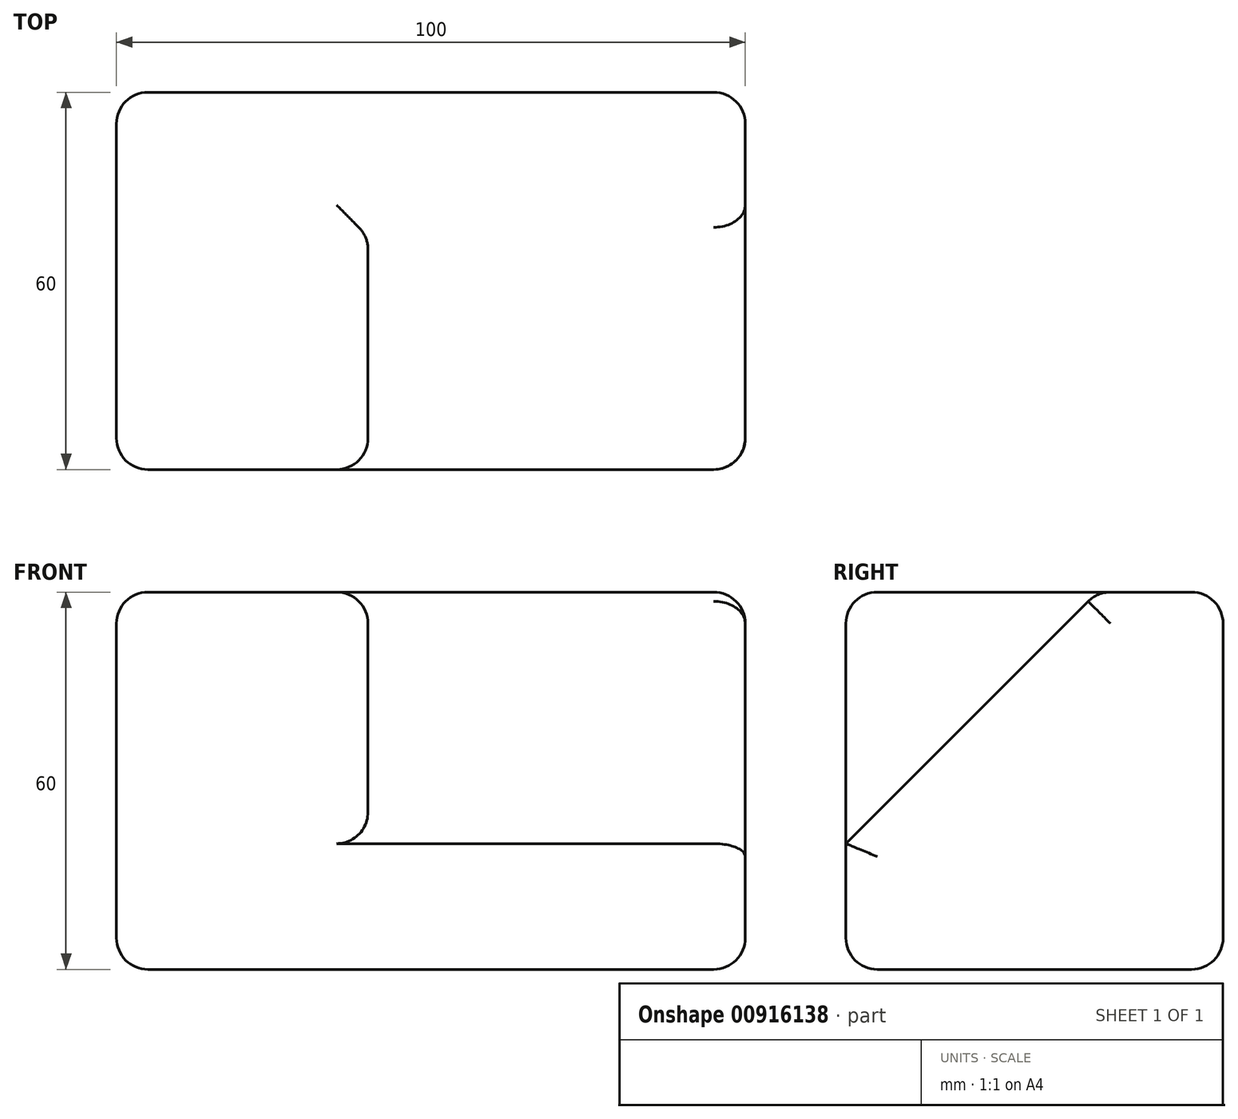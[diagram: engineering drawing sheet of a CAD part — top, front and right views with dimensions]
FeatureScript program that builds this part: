
annotation { "Feature Type Name" : "Feature", "Feature Type Description" : "" }
export const myFeature = defineFeature(function(context is Context, id is Id, definition is map)
    precondition{}
    {
        {
            var Q0;
            Q0=qCreatedBy(makeId("Top.planeOp"),FACE);
            var sketch = newSketch(context, id + "F0", { "sketchPlane" : qUnion([Q0])});
            skLineSegment(sketch, "E0.right", {"start": v(2540, 0) * mm, "end": v(2540, -51.36) * mm});
            skLineSegment(sketch, "E1.bottom", {"start": v(0, 0) * mm, "end": v(100, 0) * mm});
            skLineSegment(sketch, "E1.top", {"start": v(0, -60) * mm, "end": v(100, -60) * mm});
            skLineSegment(sketch, "E1.left", {"start": v(0, 0) * mm, "end": v(0, -60) * mm});
            skLineSegment(sketch, "E1.right", {"start": v(100, 0) * mm, "end": v(100, -60) * mm});
            skSolve(sketch);
        }
        {
            var Q0;
            Q0 = qSketchRegion(id + "F0", true);
            var Q1;
            Q1=makeQuery(id+"F0.imprint","IMPRINT",FACE,{"disambiguationData":[TD([[makeQuery(id+"F0.imprint","IMPRINT",EDGE,{"derivedFrom":sQuery(id+"F0.wireOp",EDGE,"E1.bottom")}),-1.0]])]});
            extrude(context, id + "F1", {"entities" : qUnion([Q0, Q1]), "depth" : 20 * mm, "offsetDistance" : 25 * mm});
        }
        {
            var Q0;
            Q0=makeQuery(id+"F1.opExtrude","CAP_FACE",FACE,{"disambiguationData":[OSD([sQuery(id+"F0.wireOp",EDGE,"E1.bottom"),sQuery(id+"F0.wireOp",EDGE,"E1.top"),sQuery(id+"F0.wireOp",EDGE,"E1.left"),sQuery(id+"F0.wireOp",EDGE,"E1.right")])],"isStart":false});
            var sketch = newSketch(context, id + "F2", { "sketchPlane" : qUnion([Q0])});
            skLineSegment(sketch, "E2", {"start": v(100, -20) * mm, "end": v(40, -20) * mm});
            skLineSegment(sketch, "E3", {"start": v(40, -20) * mm, "end": v(40, -60) * mm});
            skPoint(sketch, "E3.endSnap0", {"position": v(50, -60) * mm});
            skSolve(sketch);
        }
        {
            var Q0;
            Q0 = qSketchRegion(id + "F2", true);
            var Q1;
            {var subQ3=sQuery(id+"F2.wireOp",EDGE,"E2");Q1=makeQuery(id+"F2.imprint","IMPRINT",FACE,{"disambiguationData":[TD([[makeQuery(id+"F2.imprint","IMPRINT",EDGE,{"derivedFrom":subQ3}),-1.0]])]});}
            extrude(context, id + "F3", {"entities" : qUnion([Q0, Q1]), "operationType" : NewBodyOperationType.ADD, "depth" : 40 * mm, "offsetDistance" : 25 * mm});
        }
        {
            var Q0;
            Q0=makeQuery(id+"F3.opExtrude","SWEPT_FACE",FACE,{"disambiguationData":[OSD([sQuery(id+"F2.wireOp",EDGE,"E3")])]});
            var sketch = newSketch(context, id + "F4", { "sketchPlane" : qUnion([Q0])});
            skLineSegment(sketch, "E4", {"start": v(-60, 20) * mm, "end": v(-20, 60) * mm});
            skSolve(sketch);
        }
        {
            var Q0;
            Q0=makeQuery(id+"F4.imprint","IMPRINT",FACE,{"disambiguationData":[TD([[makeQuery(id+"F4.imprint","IMPRINT",EDGE,{"derivedFrom":sQuery(id+"F4.wireOp",EDGE,"E4")}),-1.0]])]});
            extrude(context, id + "F5", {"entities" : qUnion([Q0]), "operationType" : NewBodyOperationType.ADD, "depth" : 60 * mm, "offsetDistance" : 25 * mm});
        }
        {
            var Q0;
            Q0=makeQuery(id+"F3.opExtrude","CAP_EDGE",EDGE,{"disambiguationData":[OSD([sQuery(id+"F0.wireOp",EDGE,"E1.top")])],"isStart":false});
            var Q1;
            Q1=makeQuery(id+"F3.opExtrude","SWEPT_EDGE",EDGE,{"disambiguationData":[OSD([sQuery(id+"F0.wireOp",EDGE,"E1.top"),sQuery(id+"F2.wireOp",EDGE,"E3")])]});
            var Q2;
            Q2=makeQuery(id+"F3.opExtrude","CAP_EDGE",EDGE,{"disambiguationData":[OSD([sQuery(id+"F2.wireOp",EDGE,"E3")])],"isStart":false});
            var Q3;
            Q3=makeQuery(id+"F5.opExtrude","CAP_EDGE",EDGE,{"disambiguationData":[OSD([sQuery(id+"F4.wireOp",EDGE,"E4")])],"isStart":true});
            var Q4;
            Q4=makeQuery(id+"F5.opExtrude","CAP_EDGE",EDGE,{"disambiguationData":[OSD([sQuery(id+"F4.wireOp",EDGE,"E4")])],"isStart":false});
            var Q5;
            Q5=makeQuery(id+"F1.opExtrude","SWEPT_EDGE",EDGE,{"disambiguationData":[OSD([sQuery(id+"F0.wireOp",EDGE,"E1.top"),sQuery(id+"F0.wireOp",EDGE,"E1.right")])]});
            var Q6;
            Q6=makeQuery(id+"F1.opExtrude","CAP_EDGE",EDGE,{"disambiguationData":[OSD([sQuery(id+"F0.wireOp",EDGE,"E1.right")])],"isStart":true});
            var Q7;
            Q7=makeQuery(id+"F1.opExtrude","CAP_EDGE",EDGE,{"disambiguationData":[OSD([sQuery(id+"F0.wireOp",EDGE,"E1.top")])],"isStart":true});
            var Q8;
            Q8=makeQuery(id+"F3.opExtrude","CAP_EDGE",EDGE,{"disambiguationData":[OSD([sQuery(id+"F0.wireOp",EDGE,"E1.bottom")])],"isStart":false});
            var Q9;
            Q9=makeQuery(id+"F3.opExtrude","CAP_EDGE",EDGE,{"disambiguationData":[OSD([sQuery(id+"F0.wireOp",EDGE,"E1.left")])],"isStart":false});
            var Q10;
            {var subQ0=sQuery(id+"F0.wireOp",EDGE,"E1.right");var subQ1=sQuery(id+"F0.wireOp",EDGE,"E1.bottom");Q10=makeQuery(id+"F3.boolean.opBoolean","MERGE",EDGE,{"derivedFrom":[makeQuery(id+"F1.opExtrude","SWEPT_EDGE",EDGE,{"disambiguationData":[OSD([subQ1,subQ0])]}),makeQuery(id+"F3.opExtrude","SWEPT_EDGE",EDGE,{"disambiguationData":[OSD([subQ1,subQ0])]})]});}
            var Q11;
            {var subQ0=sQuery(id+"F0.wireOp",EDGE,"E1.left");var subQ1=sQuery(id+"F0.wireOp",EDGE,"E1.bottom");Q11=makeQuery(id+"F3.boolean.opBoolean","MERGE",EDGE,{"derivedFrom":[makeQuery(id+"F1.opExtrude","SWEPT_EDGE",EDGE,{"disambiguationData":[OSD([subQ1,subQ0])]}),makeQuery(id+"F3.opExtrude","SWEPT_EDGE",EDGE,{"disambiguationData":[OSD([subQ1,subQ0])]})]});}
            var Q12;
            Q12=makeQuery(id+"F1.opExtrude","CAP_EDGE",EDGE,{"disambiguationData":[OSD([sQuery(id+"F0.wireOp",EDGE,"E1.bottom")])],"isStart":true});
            var Q13;
            Q13=makeQuery(id+"F1.opExtrude","CAP_EDGE",EDGE,{"disambiguationData":[OSD([sQuery(id+"F0.wireOp",EDGE,"E1.left")])],"isStart":true});
            fillet(context, id + "F6", {"entities" : qUnion([Q0, Q1, Q2, Q3, Q4, Q5, Q6, Q7, Q8, Q9, Q10, Q11, Q12, Q13]), "radius" : 5 * mm, "tangentPropagation" : true, "allowEdgeOverflow" : false});
        }
        {
            var Q0;
            Q0=makeQuery(id+"F3.opExtrude","CAP_EDGE",EDGE,{"disambiguationData":[OSD([sQuery(id+"F0.wireOp",EDGE,"E1.right")])],"isStart":false});
            var Q1;
            {var subQ0=sQuery(id+"F0.wireOp",EDGE,"E1.left");var subQ1=sQuery(id+"F0.wireOp",EDGE,"E1.top");Q1=makeQuery(id+"F3.boolean.opBoolean","MERGE",EDGE,{"derivedFrom":[makeQuery(id+"F1.opExtrude","SWEPT_EDGE",EDGE,{"disambiguationData":[OSD([subQ1,subQ0])]}),makeQuery(id+"F3.opExtrude","SWEPT_EDGE",EDGE,{"disambiguationData":[OSD([subQ1,subQ0])]})]});}
            fillet(context, id + "F7", {"entities" : qUnion([Q0, Q1]), "radius" : 5 * mm, "tangentPropagation" : true, "allowEdgeOverflow" : false});
        }
    });
